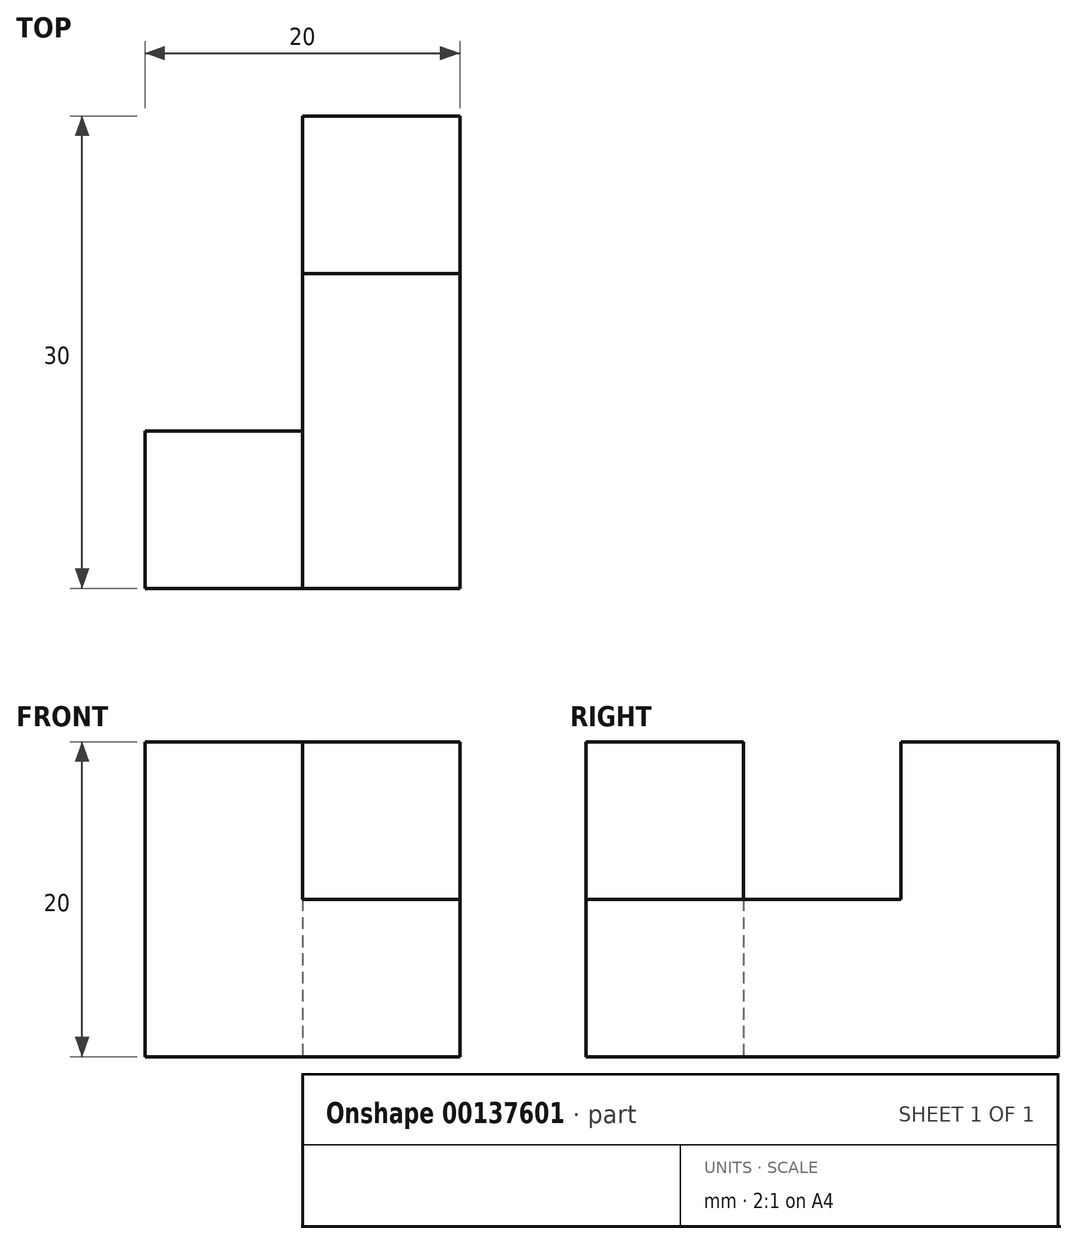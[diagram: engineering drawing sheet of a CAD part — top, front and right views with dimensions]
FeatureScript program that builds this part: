
annotation { "Feature Type Name" : "Feature", "Feature Type Description" : "" }
export const myFeature = defineFeature(function(context is Context, id is Id, definition is map)
    precondition{}
    {
        {
            var Q0;
            Q0=qCreatedBy(makeId("Front.planeOp"),FACE);
            var sketch = newSketch(context, id + "F0", { "sketchPlane" : qUnion([Q0])});
            skLineSegment(sketch, "E0", {"start": v(-20, 20) * mm, "end": v(-20, 0) * mm});
            skLineSegment(sketch, "E1", {"start": v(-20, 0) * mm, "end": v(0, 0) * mm});
            skLineSegment(sketch, "E2", {"start": v(0, 0) * mm, "end": v(0, 10) * mm});
            skLineSegment(sketch, "E3", {"start": v(0, 10) * mm, "end": v(-10, 10) * mm});
            skLineSegment(sketch, "E4", {"start": v(-10, 10) * mm, "end": v(-10, 20) * mm});
            skLineSegment(sketch, "E5", {"start": v(-10, 20) * mm, "end": v(-20, 20) * mm});
            skSolve(sketch);
        }
        {
            var Q0;
            Q0=makeQuery(id+"F0.imprint","IMPRINT",FACE,{"disambiguationData":[TD([[makeQuery(id+"F0.imprint","IMPRINT",EDGE,{"derivedFrom":sQuery(id+"F0.wireOp",EDGE,"E0")}),1.0]])]});
            extrude(context, id + "F1", {"entities" : qUnion([Q0]), "depth" : 10 * mm});
        }
        {
            var Q0;
            Q0=qCreatedBy(makeId("Right.planeOp"),FACE);
            var sketch = newSketch(context, id + "F2", { "sketchPlane" : qUnion([Q0])});
            skLineSegment(sketch, "E6", {"start": v(0, 0) * mm, "end": v(20, 0) * mm});
            skLineSegment(sketch, "E7", {"start": v(20, 0) * mm, "end": v(20, 20) * mm});
            skLineSegment(sketch, "E8", {"start": v(20, 20) * mm, "end": v(10, 20) * mm});
            skLineSegment(sketch, "E9", {"start": v(10, 20) * mm, "end": v(10, 10) * mm});
            skLineSegment(sketch, "E10", {"start": v(10, 10) * mm, "end": v(0, 10) * mm});
            skLineSegment(sketch, "E11", {"start": v(0, 10) * mm, "end": v(0, 0) * mm});
            skSolve(sketch);
        }
        {
            var Q0;
            Q0=makeQuery(id+"F2.imprint","IMPRINT",FACE,{"disambiguationData":[TD([[makeQuery(id+"F2.imprint","IMPRINT",EDGE,{"derivedFrom":sQuery(id+"F2.wireOp",EDGE,"E6")}),1.0]])]});
            extrude(context, id + "F3", {"entities" : qUnion([Q0]), "operationType" : NewBodyOperationType.ADD, "oppositeDirection" : true, "depth" : 10 * mm});
        }
    });
